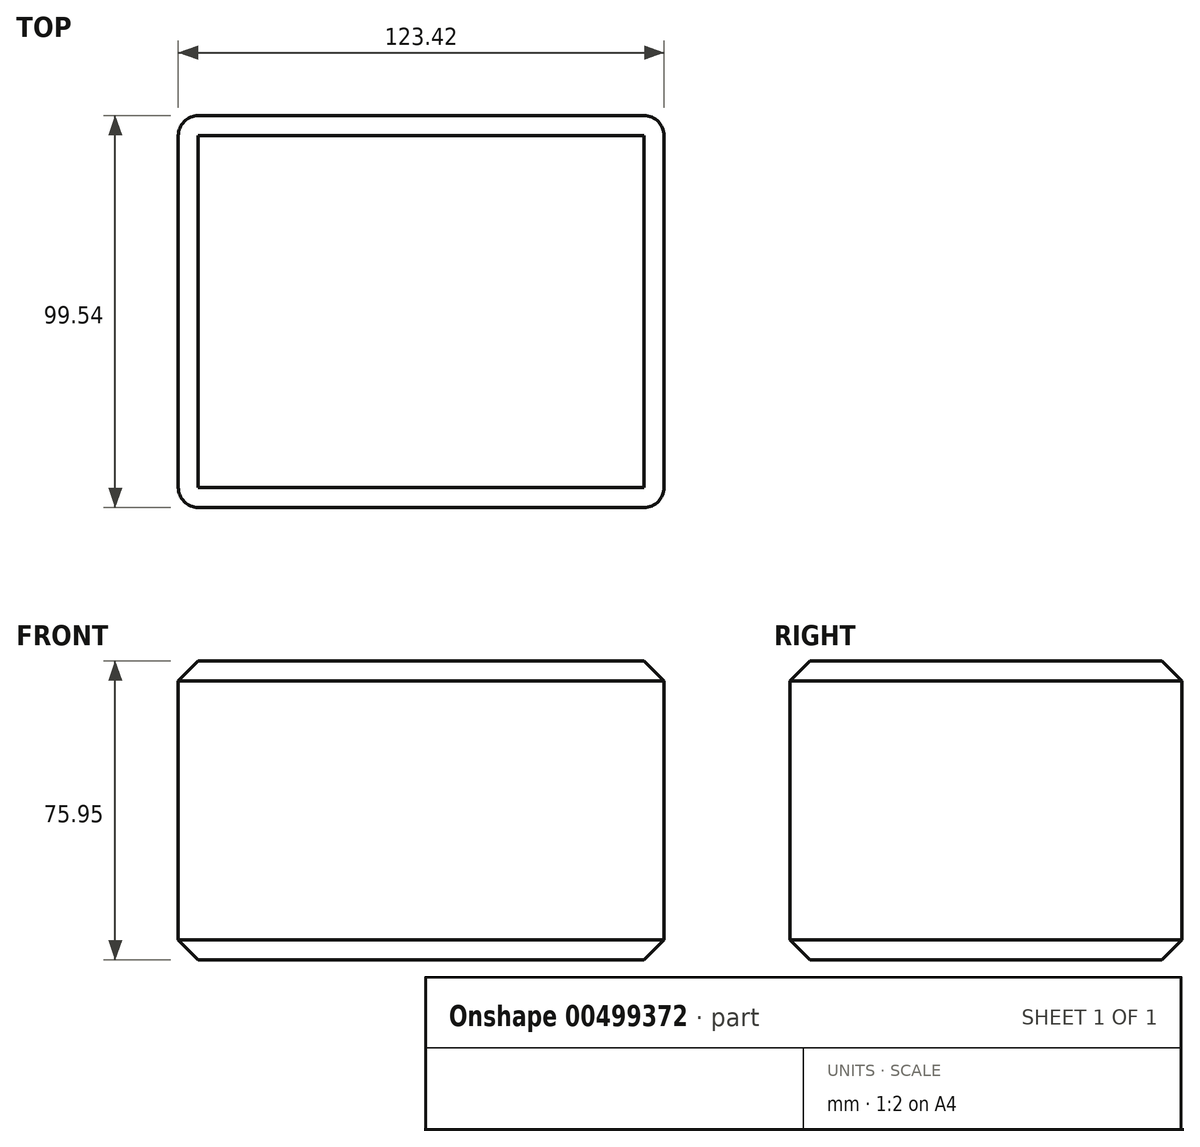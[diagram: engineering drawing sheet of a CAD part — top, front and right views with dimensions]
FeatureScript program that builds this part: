
annotation { "Feature Type Name" : "Feature", "Feature Type Description" : "" }
export const myFeature = defineFeature(function(context is Context, id is Id, definition is map)
    precondition{}
    {
        {
            var Q0;
            Q0=qCreatedBy(makeId("Top.planeOp"),FACE);
            var sketch = newSketch(context, id + "F0", { "sketchPlane" : qUnion([Q0])});
            skLineSegment(sketch, "E0.bottom", {"start": v(-50.43, 48.73) * mm, "end": v(73, 48.73) * mm});
            skLineSegment(sketch, "E0.top", {"start": v(-50.43, -50.81) * mm, "end": v(73, -50.81) * mm});
            skLineSegment(sketch, "E0.left", {"start": v(-50.43, 48.73) * mm, "end": v(-50.43, -50.81) * mm});
            skLineSegment(sketch, "E0.right", {"start": v(73, 48.73) * mm, "end": v(73, -50.81) * mm});
            skSolve(sketch);
        }
        {
            var Q0;
            Q0 = qSketchRegion(id + "F0", true);
            extrude(context, id + "F1", {"entities" : qUnion([Q0]), "depth" : 75.95 * mm});
        }
        {
            var Q0;
            Q0=makeQuery(id+"F1.opExtrude","SWEPT_EDGE",EDGE,{"disambiguationData":[OSD([sQuery(id+"F0.wireOp",EDGE,"E0.bottom"),sQuery(id+"F0.wireOp",EDGE,"E0.right")])]});
            var Q1;
            Q1=makeQuery(id+"F1.opExtrude","SWEPT_EDGE",EDGE,{"disambiguationData":[OSD([sQuery(id+"F0.wireOp",EDGE,"E0.bottom"),sQuery(id+"F0.wireOp",EDGE,"E0.left")])]});
            var Q2;
            Q2=makeQuery(id+"F1.opExtrude","SWEPT_EDGE",EDGE,{"disambiguationData":[OSD([sQuery(id+"F0.wireOp",EDGE,"E0.top"),sQuery(id+"F0.wireOp",EDGE,"E0.right")])]});
            var Q3;
            Q3=makeQuery(id+"F1.opExtrude","SWEPT_EDGE",EDGE,{"disambiguationData":[OSD([sQuery(id+"F0.wireOp",EDGE,"E0.top"),sQuery(id+"F0.wireOp",EDGE,"E0.left")])]});
            fillet(context, id + "F2", {"entities" : qUnion([Q0, Q1, Q2, Q3]), "radius" : 5.08 * mm, "tangentPropagation" : true, "allowEdgeOverflow" : false});
        }
        {
            var Q0;
            Q0=makeQuery(id+"F1.opExtrude","CAP_EDGE",EDGE,{"disambiguationData":[OSD([sQuery(id+"F0.wireOp",EDGE,"E0.left")])],"isStart":false});
            var Q1;
            Q1=makeQuery(id+"F1.opExtrude","CAP_EDGE",EDGE,{"disambiguationData":[OSD([sQuery(id+"F0.wireOp",EDGE,"E0.left")])],"isStart":true});
            chamfer(context, id + "F3", {"entities" : qUnion([Q0, Q1]), "width" : 5.08 * mm, "tangentPropagation" : true});
        }
    });
